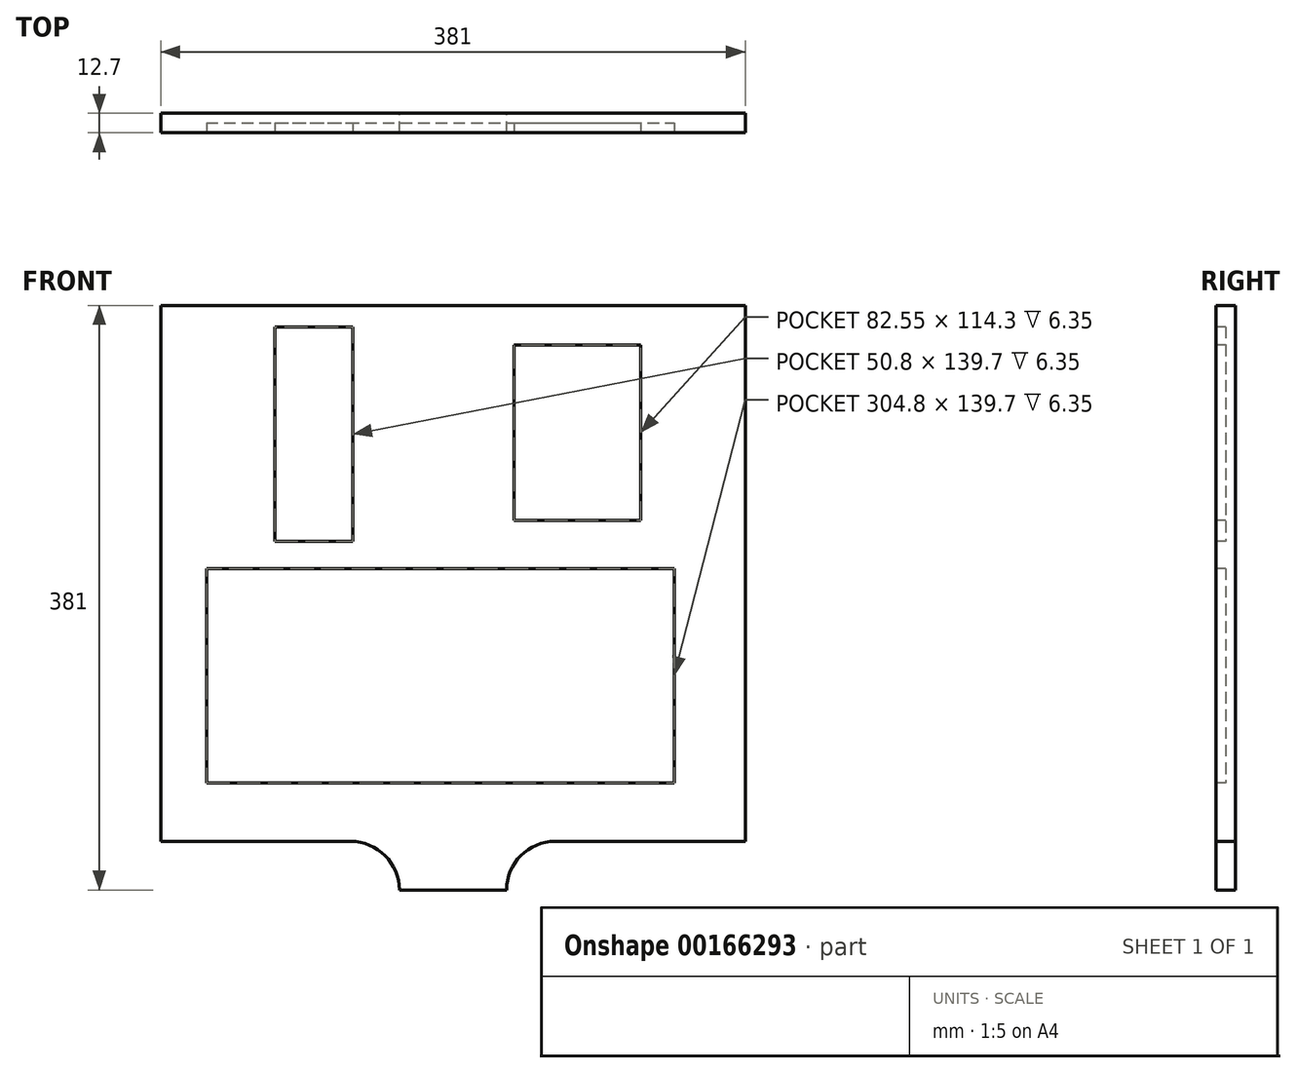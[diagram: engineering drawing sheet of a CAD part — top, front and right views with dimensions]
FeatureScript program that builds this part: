
annotation { "Feature Type Name" : "Feature", "Feature Type Description" : "" }
export const myFeature = defineFeature(function(context is Context, id is Id, definition is map)
    precondition{}
    {
        {
            var Q0;
            Q0=qCreatedBy(makeId("Front.planeOp"),FACE);
            var sketch = newSketch(context, id + "F0", { "sketchPlane" : qUnion([Q0])});
            skLineSegment(sketch, "E0.bottom", {"start": v(-75.17, 76.9) * mm, "end": v(305.83, 76.9) * mm});
            skLineSegment(sketch, "E0.top", {"start": v(-75.17, -304.1) * mm, "end": v(305.83, -304.1) * mm});
            skLineSegment(sketch, "E0.left", {"start": v(-75.17, 76.9) * mm, "end": v(-75.17, -304.1) * mm});
            skLineSegment(sketch, "E0.right", {"start": v(305.83, 76.9) * mm, "end": v(305.83, -304.1) * mm});
            skLineSegment(sketch, "E1", {"start": v(-75.17, -304.1) * mm, "end": v(115.33, -304.1) * mm});
            skLineSegment(sketch, "E2", {"start": v(115.33, -304.1) * mm, "end": v(305.83, -304.1) * mm});
            skLineSegment(sketch, "E3", {"start": v(115.33, -304.1) * mm, "end": v(150.26, -304.1) * mm});
            skLineSegment(sketch, "E4", {"start": v(115.33, -304.1) * mm, "end": v(80.4, -304.1) * mm});
            skLineSegment(sketch, "E5", {"start": v(80.4, -304.1) * mm, "end": v(48.66, -304.1) * mm});
            skLineSegment(sketch, "E6", {"start": v(150.26, -304.1) * mm, "end": v(182, -304.1) * mm});
            skCircle(sketch, "E7", {"center": v(48.66, -304.1) * mm, "radius": 31.75 * mm});
            skCircle(sketch, "E8", {"center": v(182, -304.1) * mm, "radius": 31.75 * mm});
            skLineSegment(sketch, "E9", {"start": v(48.66, -272.35) * mm, "end": v(-75.17, -272.35) * mm});
            skLineSegment(sketch, "E10", {"start": v(182, -272.35) * mm, "end": v(305.83, -272.35) * mm});
            skSolve(sketch);
        }
        {
            var Q0;
            Q0=makeQuery(id+"F0.imprint","IMPRINT",FACE,{"disambiguationData":[TD([[makeQuery(id+"F0.imprint","IMPRINT",EDGE,{"derivedFrom":sQuery(id+"F0.wireOp",EDGE,"E0.bottom")}),-1.0]])]});
            extrude(context, id + "F1", {"entities" : qUnion([Q0]), "depth" : 12.7 * mm});
        }
        {
            var Q0;
            Q0=makeQuery(id+"F1.opExtrude","CAP_FACE",FACE,{"disambiguationData":[OSD([sQuery(id+"F0.wireOp",EDGE,"E0.bottom"),sQuery(id+"F0.wireOp",EDGE,"E0.top"),sQuery(id+"F0.wireOp",EDGE,"E0.left"),sQuery(id+"F0.wireOp",EDGE,"E0.right")])],"isStart":false});
            var sketch = newSketch(context, id + "F2", { "sketchPlane" : qUnion([Q0])});
            skLineSegment(sketch, "E11.bottom", {"start": v(-0.85, 62.88) * mm, "end": v(49.95, 62.88) * mm});
            skLineSegment(sketch, "E11.top", {"start": v(-0.85, -76.82) * mm, "end": v(49.95, -76.82) * mm});
            skLineSegment(sketch, "E11.left", {"start": v(-0.85, 62.88) * mm, "end": v(-0.85, -76.82) * mm});
            skLineSegment(sketch, "E11.right", {"start": v(49.95, 62.88) * mm, "end": v(49.95, -76.82) * mm});
            skLineSegment(sketch, "E12.bottom", {"start": v(155.2, 51.17) * mm, "end": v(237.75, 51.17) * mm});
            skLineSegment(sketch, "E12.top", {"start": v(155.2, -63.13) * mm, "end": v(237.75, -63.13) * mm});
            skLineSegment(sketch, "E12.left", {"start": v(155.2, 51.17) * mm, "end": v(155.2, -63.13) * mm});
            skLineSegment(sketch, "E12.right", {"start": v(237.75, 51.17) * mm, "end": v(237.75, -63.13) * mm});
            skLineSegment(sketch, "E13.bottom", {"start": v(-45.3, -94.53) * mm, "end": v(259.5, -94.53) * mm});
            skLineSegment(sketch, "E13.top", {"start": v(-45.3, -234.23) * mm, "end": v(259.5, -234.23) * mm});
            skLineSegment(sketch, "E13.left", {"start": v(-45.3, -94.53) * mm, "end": v(-45.3, -234.23) * mm});
            skLineSegment(sketch, "E13.right", {"start": v(259.5, -94.53) * mm, "end": v(259.5, -234.23) * mm});
            skSolve(sketch);
        }
        {
            var Q0;
            Q0=makeQuery(id+"F2.imprint","IMPRINT",FACE,{"disambiguationData":[TD([[makeQuery(id+"F2.imprint","IMPRINT",EDGE,{"derivedFrom":sQuery(id+"F2.wireOp",EDGE,"E13.bottom")}),-1.0]])]});
            var Q1;
            Q1=makeQuery(id+"F2.imprint","IMPRINT",FACE,{"disambiguationData":[TD([[makeQuery(id+"F2.imprint","IMPRINT",EDGE,{"derivedFrom":sQuery(id+"F2.wireOp",EDGE,"E11.bottom")}),-1.0]])]});
            var Q2;
            Q2=makeQuery(id+"F2.imprint","IMPRINT",FACE,{"disambiguationData":[TD([[makeQuery(id+"F2.imprint","IMPRINT",EDGE,{"derivedFrom":sQuery(id+"F2.wireOp",EDGE,"E12.bottom")}),-1.0]])]});
            extrude(context, id + "F3", {"entities" : qUnion([Q0, Q1, Q2]), "operationType" : NewBodyOperationType.REMOVE, "oppositeDirection" : true, "depth" : 6.35 * mm});
        }
    });
